# Revit family: 44a5e479_73ad_4a02_ae60_61a08da23758
name_source: partatom
category: Generic Models
revit_build: Autodesk Revit Architecture 2015 (Build: 20140606_1530(x64)
units: mm (PartAtom-declared; Revit-internal decimal feet)

## types (1)
- Default
    BIMobject category = Basins
    BOSUseNativeGeometries = 0
    Brand url = http://www.duravit.com
    Date of publishing = 1/11/2017
    Edition number = 1
    IFC Classification = Sanitary Terminal
    Installation instructions = http://pro.duravit.com
    Manufacturer name = DURAVIT
    Masterformat 2014 Code = 22 45 26
    Masterformat 2014 Description = Eye/Face Wash Equipment
    NBS Reference Code = 31-76
    NBS Reference Description = Sanitary Dispensing And Disposal Units
    Nominal height = 0
    Nominal width = 615
    OmniClass Code = 23-19 31 17
    OmniClass Description = Sanitary Room Units
    Product Guid = 44e59a94-aaa2-4fc3-abc8-8f57632cb0ed
    Product SKU = durastyle-vanity-basin-037462
    Product certification = http://pro.duravit.com
    Product data url = https://bimobject.com
    Product family = DuraStyle
    Product group = Vanity basin
    Product name = DuraStyle Vanity basin 037462
    Product url = http://pro.duravit.com
    QR code = http://bimobject.com
    Technical description = http://pro.duravit.com
    UNSPSC Code = 301815
    Uniclass 1.4 Code = L721
    Uniclass 1.4 Description = Sanitary equipment
    Uniclass 2.0 Code = PR-31-76
    Uniclass 2.0 Description = Sanitary Dispensing And Disposal Units
    Uniclass 2015 Code = Pr_40_20_96_70
    Uniclass 2015 Name = Recessed wash basins
    Uniformat II Code = D2010
    Uniformat II Description = Plumbing Fixtures
    Weight Net (Kg) = 12.5

## geometry (parser evidence)
native form markers: Sweep x3
no freeform markers — native parametric forms only
